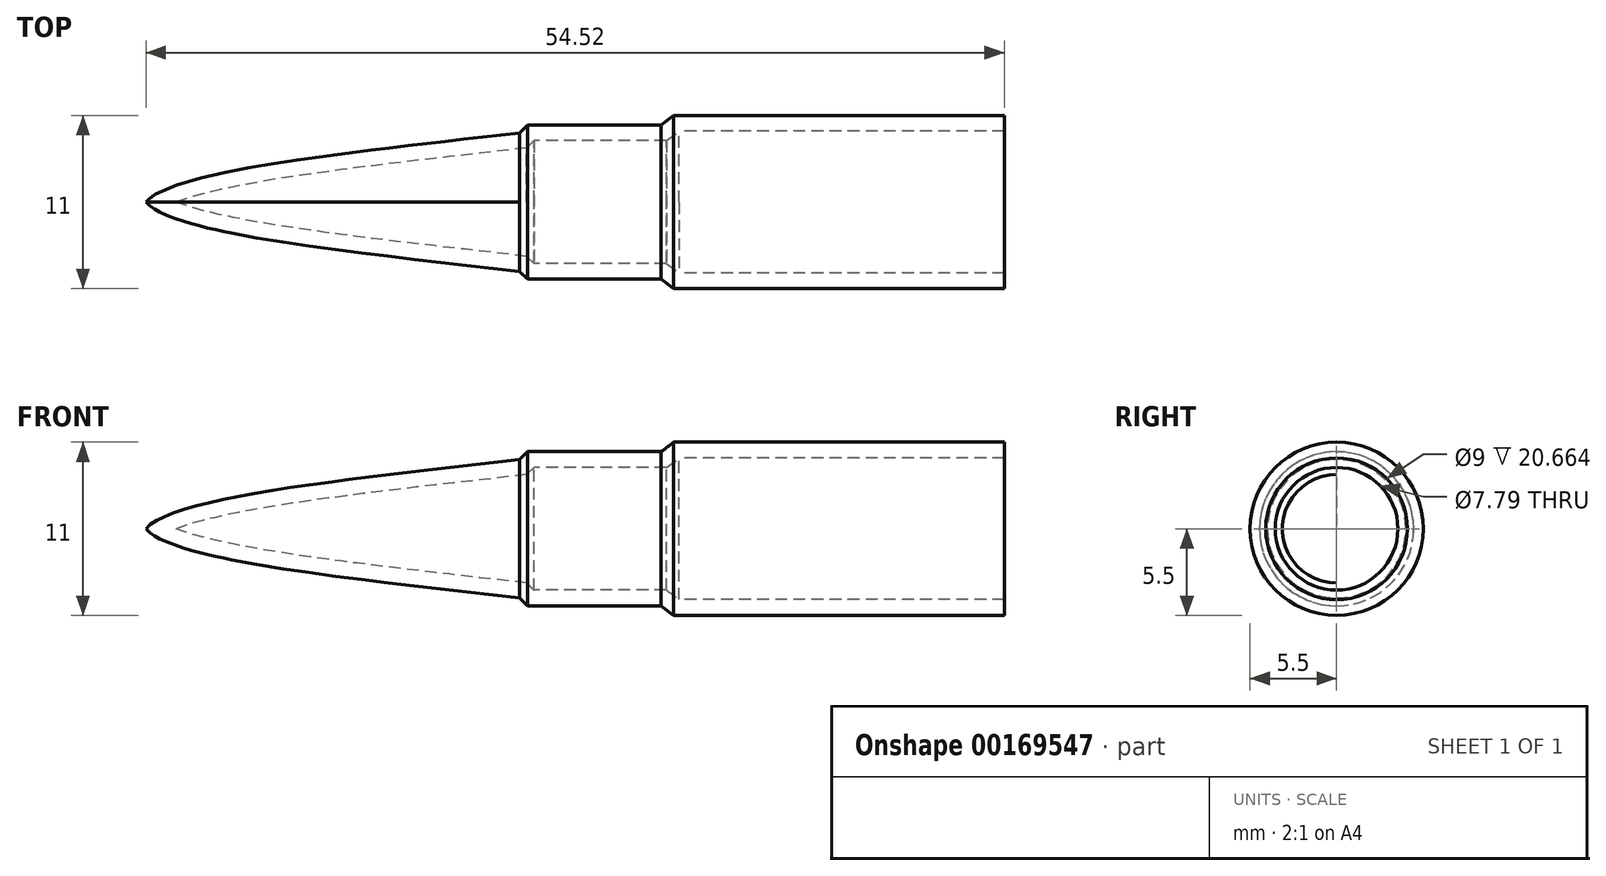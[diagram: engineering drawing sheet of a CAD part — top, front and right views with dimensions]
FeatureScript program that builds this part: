
annotation { "Feature Type Name" : "Feature", "Feature Type Description" : "" }
export const myFeature = defineFeature(function(context is Context, id is Id, definition is map)
    precondition{}
    {
        {
            var Q0;
            Q0=qCreatedBy(makeId("Front.planeOp"),FACE);
            var sketch = newSketch(context, id + "F0", { "sketchPlane" : qUnion([Q0])});
            skLineSegment(sketch, "E0", {"start": v(0, 0) * mm, "end": v(0, 5.5) * mm});
            skLineSegment(sketch, "E1", {"start": v(0, 5.5) * mm, "end": v(-21, 5.5) * mm});
            skLineSegment(sketch, "E2", {"start": v(-21, 5.5) * mm, "end": v(-21.8, 4.9) * mm});
            skLineSegment(sketch, "E3", {"start": v(-21.8, 4.9) * mm, "end": v(-30.8, 4.9) * mm});
            skLineSegment(sketch, "E4", {"start": v(-30.8, 4.9) * mm, "end": v(-30.8, 4.4) * mm});
            skLineSegment(sketch, "E5", {"start": v(-54.52, 0) * mm, "end": v(0, 0) * mm});
            skFitSpline(sketch, "E6", {"points": [v(-30.8, 4.4) * mm, v(-54.52, 0) * mm, v(-54.52, -1.81) * mm], "startDerivative": vector(-40.13, -4.62) * mm, "endDerivative": vector(3.13, -8.43) * mm});
            skPoint(sketch, "E7", {"position": v(0, 0) * mm});
            skSolve(sketch);
        }
        {
            var Q0;
            Q0 = qSketchRegion(id + "F0", true);
            var Q1;
            Q1=sQuery(id+"F0.wireOp",EDGE,"E5");
            revolve(context, id + "F1", {"entities" : qUnion([Q0]), "axis" : qUnion([Q1]), "revolveType" : RevolveType.FULL});
        }
        {
            var Q0;
            Q0=makeQuery(id+"F1.opRevolve","SWEPT_EDGE",EDGE,{"disambiguationData":[OSD([sQuery(id+"F0.wireOp",EDGE,"E3"),sQuery(id+"F0.wireOp",EDGE,"E4")])]});
            chamfer(context, id + "F2", {"entities" : qUnion([Q0]), "width" : 0.5 * mm, "tangentPropagation" : true});
        }
        {
            var Q0;
            Q0=makeQuery(id+"F1.opRevolve","SWEPT_FACE",FACE,{"disambiguationData":[OSD([sQuery(id+"F0.wireOp",EDGE,"E0")])]});
            shell(context, id + "F3", {"entities" : qUnion([Q0]), "thickness" : 1 * mm});
        }
    });
